FREECAD ASSEMBLY — COMPONENT RECIPES ("Mover")

This assembly document has 35 components, labeled P0..P34 below (a component is one placed body or linked part). 0 of them carry a construction recipe — the FreeCAD feature program that regenerates the part from scratch, quoted from this document or its linked companion documents; the rest are supplied as boundary geometry only. No exploded tour is included for this assembly.
COMPONENT P0 — geometry summary ("B-Mount Washer L"; no construction recipe available for this part):
  bounding box: 20.0 x 20.0 x 4.0 mm
  tessellated surface: 856 triangles
  volume: 1162 mm^3 (73% of its bounding box)
  symmetry: revolution-symmetric about the x axis through its bounding-box center; 2-fold rotationally symmetric about the y axis; 2-fold rotationally symmetric about the z axis; mirror-symmetric across its y mid-plane, z mid-plane
COMPONENT P1 — geometry summary ("B-Mount Washer R"; no construction recipe available for this part):
  bounding box: 20.0 x 20.0 x 4.0 mm
  tessellated surface: 856 triangles
  volume: 1162 mm^3 (73% of its bounding box)
  symmetry: revolution-symmetric about the x axis through its bounding-box center; 2-fold rotationally symmetric about the y axis; 2-fold rotationally symmetric about the z axis; mirror-symmetric across its y mid-plane, z mid-plane
COMPONENT P2 — geometry summary ("B-Slide Bearing R"; no construction recipe available for this part):
  bounding box: 37.4 x 35.4 x 6.3 mm
  tessellated surface: 992 triangles
  volume: 6182 mm^3 (74% of its bounding box)
  symmetry: 2-fold rotationally symmetric about the x axis; mirror-symmetric across its z mid-plane
COMPONENT P3 — geometry summary ("B-Slide Bearing Wascher R"; no construction recipe available for this part):
  bounding box: 36.0 x 34.0 x 4.0 mm
  tessellated surface: 716 triangles
  volume: 4648 mm^3 (95% of its bounding box)
  symmetry: 2-fold rotationally symmetric about the x axis; mirror-symmetric across its z mid-plane
COMPONENT P4 — geometry summary ("B-Slide Bearing Wascher L"; no construction recipe available for this part):
  bounding box: 36.0 x 34.0 x 4.0 mm
  tessellated surface: 716 triangles
  volume: 4648 mm^3 (95% of its bounding box)
  symmetry: 2-fold rotationally symmetric about the x axis; mirror-symmetric across its z mid-plane
COMPONENT P5 — geometry summary ("B-Slide Bearing w. Indicator L"; no construction recipe available for this part):
  bounding box: 43.4 x 37.4 x 7.8 mm
  tessellated surface: 1,164 triangles
  volume: 6803 mm^3 (54% of its bounding box)
  symmetry: mirror-symmetric across its z mid-plane
COMPONENT P6 — geometry summary ("B-Steppersledge Switch"; no construction recipe available for this part):
  bounding box: 461.6 x 63.3 x 59.9 mm
  tessellated surface: 5,238 triangles
  volume: 82831 mm^3 (5% of its bounding box)
COMPONENT P7 — geometry summary ("B-Steppersledge basic"; no construction recipe available for this part):
  bounding box: 461.6 x 62.4 x 28.6 mm
  tessellated surface: 6,086 triangles
  volume: 75247 mm^3 (9% of its bounding box)
  symmetry: mirror-symmetric across its y mid-plane
COMPONENT P8 — geometry summary ("B-Switch Bracket"; no construction recipe available for this part):
  bounding box: 27.0 x 22.0 x 17.8 mm
  tessellated surface: 2,738 triangles
  volume: 3093 mm^3 (29% of its bounding box)
COMPONENT P9 — geometry summary ("M2.5-Mutter001"; no construction recipe available for this part):
  bounding box: 5.8 x 5.0 x 2.0 mm
  tessellated surface: 1,236 triangles
  volume: 36 mm^3 (63% of its bounding box)
  symmetry: 2-fold rotationally symmetric about the x axis; 6-fold rotationally symmetric about the y axis; 2-fold rotationally symmetric about the z axis; mirror-symmetric across its x mid-plane, y mid-plane, z mid-plane
COMPONENT P10 — geometry summary ("M2.5-Mutter002"; no construction recipe available for this part):
  bounding box: 5.8 x 5.0 x 2.0 mm
  tessellated surface: 1,236 triangles
  volume: 36 mm^3 (63% of its bounding box)
  symmetry: 2-fold rotationally symmetric about the x axis; 6-fold rotationally symmetric about the y axis; 2-fold rotationally symmetric about the z axis; mirror-symmetric across its y mid-plane, z mid-plane
COMPONENT P11 — geometry summary ("M2.5x16-Schraube001"; no construction recipe available for this part):
  bounding box: 16.0 x 4.9 x 4.9 mm
  tessellated surface: 1,548 triangles
  volume: 84 mm^3 (22% of its bounding box)
  symmetry: 6-fold rotationally symmetric about the y axis; mirror-symmetric across its x mid-plane
COMPONENT P12 — geometry summary ("M2.5x16-Schraube002"; no construction recipe available for this part):
  bounding box: 16.0 x 4.9 x 4.9 mm
  tessellated surface: 1,548 triangles
  volume: 84 mm^3 (22% of its bounding box)
  symmetry: 6-fold rotationally symmetric about the y axis; mirror-symmetric across its x mid-plane
COMPONENT P13 — geometry summary ("M5-Mutter-Stepper-001"; no construction recipe available for this part):
  bounding box: 9.2 x 8.0 x 4.0 mm
  tessellated surface: 1,604 triangles
  volume: 167 mm^3 (56% of its bounding box)
  symmetry: 2-fold rotationally symmetric about the x axis; 2-fold rotationally symmetric about the y axis; 6-fold rotationally symmetric about the z axis; mirror-symmetric across its x mid-plane
COMPONENT P14 — geometry summary ("M5-Mutter-Stepper-002"; no construction recipe available for this part):
  bounding box: 9.2 x 8.0 x 4.0 mm
  tessellated surface: 1,604 triangles
  volume: 167 mm^3 (56% of its bounding box)
  symmetry: 2-fold rotationally symmetric about the x axis; 2-fold rotationally symmetric about the y axis; 6-fold rotationally symmetric about the z axis; mirror-symmetric across its x mid-plane
COMPONENT P15 — geometry summary ("M5-Mutter-Stepper-003"; no construction recipe available for this part):
  bounding box: 9.2 x 8.0 x 4.0 mm
  tessellated surface: 1,604 triangles
  volume: 167 mm^3 (56% of its bounding box)
  symmetry: 2-fold rotationally symmetric about the x axis; 2-fold rotationally symmetric about the y axis; 6-fold rotationally symmetric about the z axis; mirror-symmetric across its x mid-plane
COMPONENT P16 — geometry summary ("M5-Mutter-Stepper-004"; no construction recipe available for this part):
  bounding box: 9.2 x 8.0 x 4.0 mm
  tessellated surface: 1,604 triangles
  volume: 167 mm^3 (56% of its bounding box)
  symmetry: 2-fold rotationally symmetric about the x axis; 2-fold rotationally symmetric about the y axis; 6-fold rotationally symmetric about the z axis; mirror-symmetric across its x mid-plane
COMPONENT P17 — geometry summary ("M5-Scheibe-Stepper-001"; no construction recipe available for this part):
  bounding box: 10.0 x 10.0 x 1.0 mm
  tessellated surface: 844 triangles
  volume: 56 mm^3 (56% of its bounding box)
  symmetry: 2-fold rotationally symmetric about the x axis; revolution-symmetric about the z axis through its bounding-box center; mirror-symmetric across its x mid-plane, y mid-plane
COMPONENT P18 — geometry summary ("M5-Scheibe-Stepper-003"; no construction recipe available for this part):
  bounding box: 10.0 x 10.0 x 1.0 mm
  tessellated surface: 844 triangles
  volume: 56 mm^3 (56% of its bounding box)
  symmetry: 2-fold rotationally symmetric about the x axis; revolution-symmetric about the z axis through its bounding-box center; mirror-symmetric across its x mid-plane, y mid-plane
COMPONENT P19 — geometry summary ("M5-Scheibe-Stepper-002"; no construction recipe available for this part):
  bounding box: 10.0 x 10.0 x 1.0 mm
  tessellated surface: 844 triangles
  volume: 56 mm^3 (56% of its bounding box)
  symmetry: 2-fold rotationally symmetric about the x axis; revolution-symmetric about the z axis through its bounding-box center; mirror-symmetric across its x mid-plane, y mid-plane
COMPONENT P20 — geometry summary ("M5-Scheibe-Stepper-004"; no construction recipe available for this part):
  bounding box: 10.0 x 10.0 x 1.0 mm
  tessellated surface: 844 triangles
  volume: 56 mm^3 (56% of its bounding box)
  symmetry: 2-fold rotationally symmetric about the x axis; revolution-symmetric about the z axis through its bounding-box center; mirror-symmetric across its x mid-plane, y mid-plane
COMPONENT P21 — geometry summary ("M5-Scheibe-Jack-001"; no construction recipe available for this part):
  bounding box: 10.0 x 10.0 x 1.0 mm
  tessellated surface: 844 triangles
  volume: 56 mm^3 (56% of its bounding box)
  symmetry: 2-fold rotationally symmetric about the x axis; revolution-symmetric about the z axis through its bounding-box center; mirror-symmetric across its x mid-plane, y mid-plane
COMPONENT P22 — geometry summary ("M5-Scheibe-Jack-002"; no construction recipe available for this part):
  bounding box: 10.0 x 10.0 x 1.0 mm
  tessellated surface: 844 triangles
  volume: 56 mm^3 (56% of its bounding box)
  symmetry: 2-fold rotationally symmetric about the x axis; revolution-symmetric about the z axis through its bounding-box center; mirror-symmetric across its x mid-plane, y mid-plane
COMPONENT P23 — geometry summary ("M5-Scheibe001"; no construction recipe available for this part):
  bounding box: 10.0 x 10.0 x 1.0 mm
  tessellated surface: 844 triangles
  volume: 56 mm^3 (56% of its bounding box)
  symmetry: 2-fold rotationally symmetric about the x axis; revolution-symmetric about the z axis through its bounding-box center; mirror-symmetric across its x mid-plane, y mid-plane
COMPONENT P24 — geometry summary ("M5-Scheibe002"; no construction recipe available for this part):
  bounding box: 10.0 x 10.0 x 1.0 mm
  tessellated surface: 844 triangles
  volume: 56 mm^3 (56% of its bounding box)
  symmetry: 2-fold rotationally symmetric about the x axis; revolution-symmetric about the z axis through its bounding-box center; mirror-symmetric across its x mid-plane, y mid-plane
COMPONENT P25 — geometry summary ("M5x12-Schraube-Stepper-001"; no construction recipe available for this part):
  bounding box: 17.0 x 8.5 x 8.5 mm
  tessellated surface: 4,488 triangles
  volume: 488 mm^3 (40% of its bounding box)
  symmetry: 6-fold rotationally symmetric about the z axis; mirror-symmetric across its x mid-plane, y mid-plane
COMPONENT P26 — geometry summary ("M5x12-Schraube-Stepper-002"; no construction recipe available for this part):
  bounding box: 17.0 x 8.5 x 8.5 mm
  tessellated surface: 4,488 triangles
  volume: 488 mm^3 (40% of its bounding box)
  symmetry: 6-fold rotationally symmetric about the z axis; mirror-symmetric across its x mid-plane, y mid-plane
COMPONENT P27 — geometry summary ("M5x12-Schraube-Stepper-003"; no construction recipe available for this part):
  bounding box: 17.0 x 8.5 x 8.5 mm
  tessellated surface: 4,488 triangles
  volume: 488 mm^3 (40% of its bounding box)
  symmetry: 6-fold rotationally symmetric about the z axis; mirror-symmetric across its x mid-plane, y mid-plane
COMPONENT P28 — geometry summary ("M5x12-Schraube-Stepper-004"; no construction recipe available for this part):
  bounding box: 17.0 x 8.5 x 8.5 mm
  tessellated surface: 4,488 triangles
  volume: 488 mm^3 (40% of its bounding box)
  symmetry: 6-fold rotationally symmetric about the z axis; mirror-symmetric across its x mid-plane, y mid-plane
COMPONENT P29 — geometry summary ("M5x16-Schraube-Jack-001"; no construction recipe available for this part):
  bounding box: 21.0 x 8.5 x 8.5 mm
  tessellated surface: 4,488 triangles
  volume: 566 mm^3 (37% of its bounding box)
  symmetry: 3-fold rotationally symmetric about the x axis; mirror-symmetric across its y mid-plane, z mid-plane
COMPONENT P30 — geometry summary ("M5x16-Schraube-Jack-002"; no construction recipe available for this part):
  bounding box: 21.0 x 8.5 x 8.5 mm
  tessellated surface: 4,488 triangles
  volume: 566 mm^3 (37% of its bounding box)
  symmetry: 3-fold rotationally symmetric about the x axis; mirror-symmetric across its y mid-plane, z mid-plane
COMPONENT P31 — geometry summary ("M5x20-Schraube001"; no construction recipe available for this part):
  bounding box: 25.0 x 8.5 x 8.5 mm
  tessellated surface: 4,488 triangles
  volume: 645 mm^3 (36% of its bounding box)
  symmetry: revolution-symmetric about the x axis through its bounding-box center; mirror-symmetric across its y mid-plane
COMPONENT P32 — geometry summary ("M5x20-Schraube002"; no construction recipe available for this part):
  bounding box: 25.0 x 8.5 x 8.5 mm
  tessellated surface: 4,488 triangles
  volume: 645 mm^3 (36% of its bounding box)
  symmetry: revolution-symmetric about the x axis through its bounding-box center; mirror-symmetric across its y mid-plane
COMPONENT P33 — geometry summary ("Microswitch"; no construction recipe available for this part):
  bounding box: 23.4 x 21.9 x 6.4 mm
  tessellated surface: 5,234 triangles
  volume: 1280 mm^3 (39% of its bounding box)
  symmetry: mirror-symmetric across its y mid-plane
COMPONENT P34 — geometry summary ("23HS45-4204S007"; no construction recipe available for this part):
  bounding box: 137.0 x 72.5 x 57.0 mm
  tessellated surface: 42,974 triangles
  volume: 333857 mm^3 (59% of its bounding box)
PROVENANCE & LICENSES
A FreeCAD (.FCStd) document from a public repository crawl; recipes are the document's own serialized feature recipes (and, for linked parts, companion documents' recipes).
License: unlicense.
